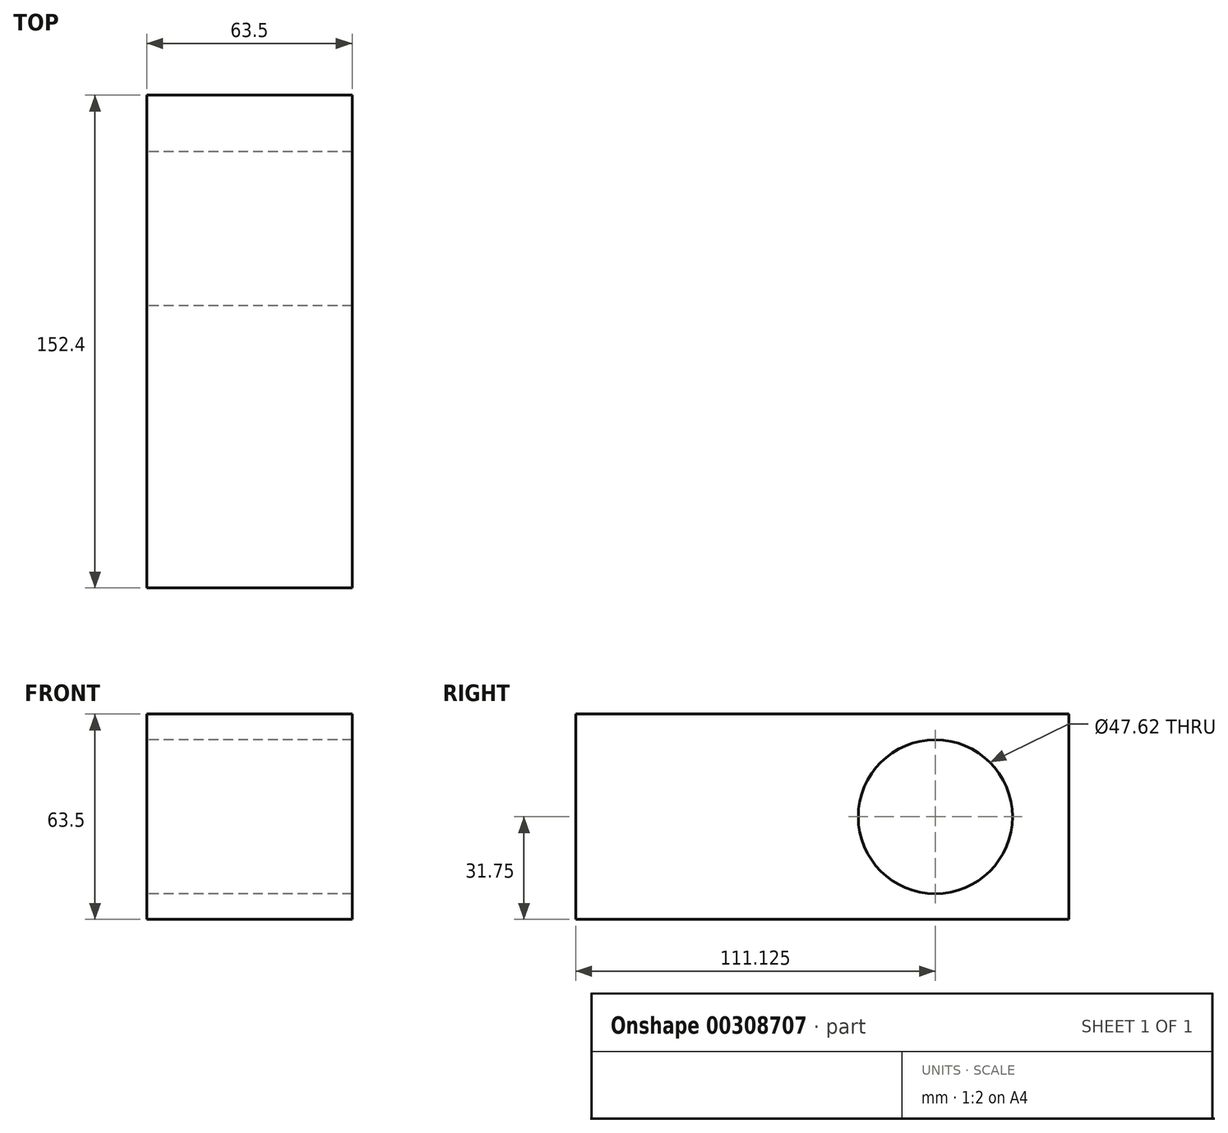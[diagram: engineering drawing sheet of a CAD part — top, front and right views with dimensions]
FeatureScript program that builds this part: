
annotation { "Feature Type Name" : "Feature", "Feature Type Description" : "" }
export const myFeature = defineFeature(function(context is Context, id is Id, definition is map)
    precondition{}
    {
        {
            var Q0;
            Q0=qCreatedBy(makeId("Front.planeOp"),FACE);
            var sketch = newSketch(context, id + "F0", { "sketchPlane" : qUnion([Q0])});
            skLineSegment(sketch, "E0", {"start": v(-31.75, 31.75) * mm, "end": v(31.75, 31.75) * mm});
            skLineSegment(sketch, "E1", {"start": v(31.75, 31.75) * mm, "end": v(31.75, -31.75) * mm});
            skLineSegment(sketch, "E2", {"start": v(31.75, -31.75) * mm, "end": v(-31.75, -31.75) * mm});
            skLineSegment(sketch, "E3", {"start": v(-31.75, -31.75) * mm, "end": v(-31.75, 31.75) * mm});
            skSolve(sketch);
        }
        {
            var Q0;
            Q0=makeQuery(id+"F0.imprint","IMPRINT",FACE,{"disambiguationData":[TD([[makeQuery(id+"F0.imprint","IMPRINT",EDGE,{"derivedFrom":sQuery(id+"F0.wireOp",EDGE,"E0")}),-1.0]])]});
            extrude(context, id + "F1", {"entities" : qUnion([Q0]), "endBound" : BoundingType.SYMMETRIC, "depth" : 152.4 * mm});
        }
        {
            var Q0;
            Q0=makeQuery(id+"F1.opExtrude","SWEPT_FACE",FACE,{"disambiguationData":[OSD([sQuery(id+"F0.wireOp",EDGE,"E3")])]});
            var sketch = newSketch(context, id + "F2", { "sketchPlane" : qUnion([Q0])});
            skPoint(sketch, "E4", {"position": v(-34.92, 0) * mm});
            skSolve(sketch);
        }
        {
            var Q0;
            Q0=sQuery(id+"F2.wireOp",VERTEX,"E4");
            var Q1;
            Q1=makeQuery(id+"F1.opExtrude","SWEPT_BODY",BODY,{"disambiguationData":[OSD([sQuery(id+"F0.wireOp",EDGE,"E0"),sQuery(id+"F0.wireOp",EDGE,"E1"),sQuery(id+"F0.wireOp",EDGE,"E2"),sQuery(id+"F0.wireOp",EDGE,"E3")])]});
            hole(context, id + "F3", {"style" : HoleStyle.SIMPLE, "endStyle" : HoleEndStyle.THROUGH, "holeDiameter" : 47.62 * mm, "tappedDepth" : 12.7 * mm, "tapClearance" : 3, "locations" : qUnion([Q0]), "scope" : qUnion([Q1])});
        }
    });
